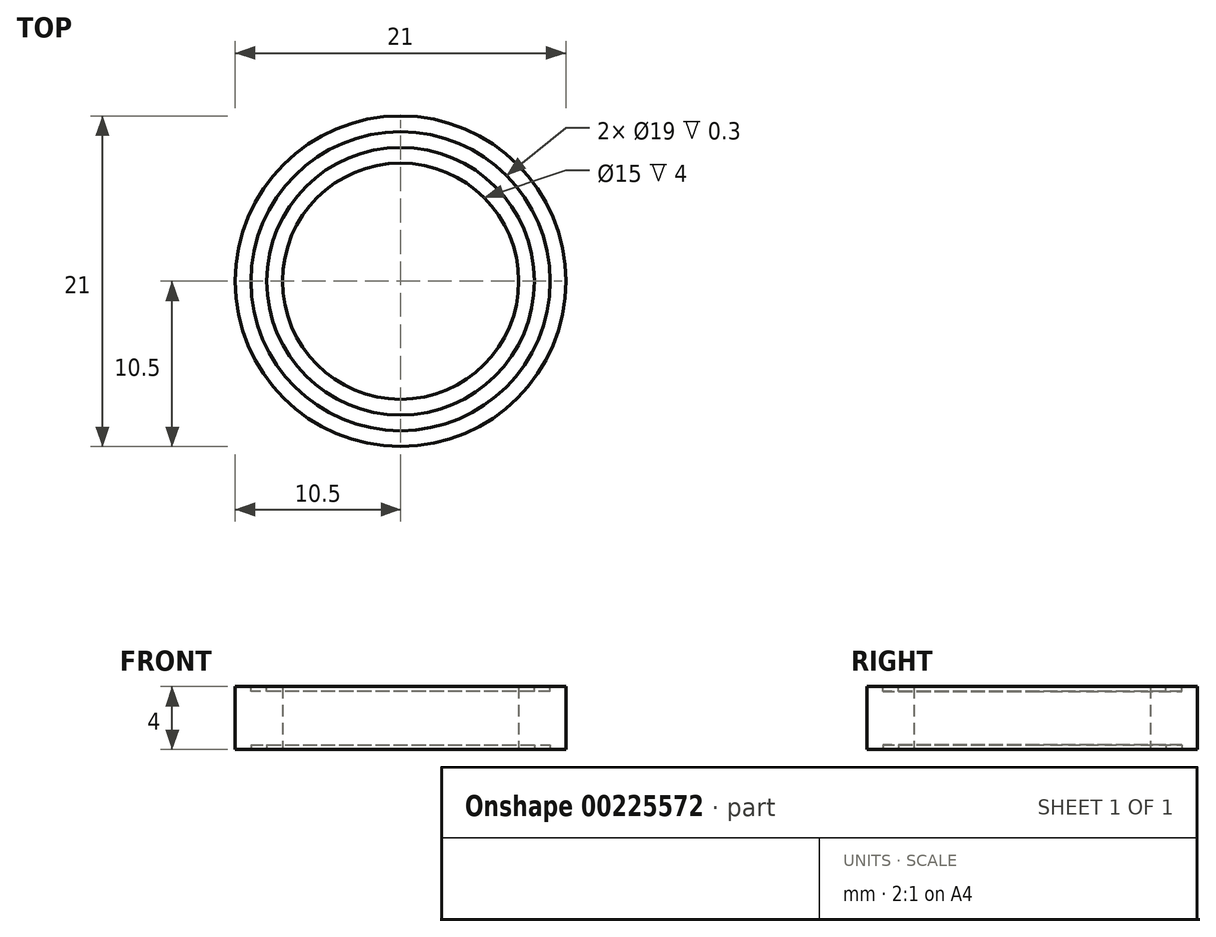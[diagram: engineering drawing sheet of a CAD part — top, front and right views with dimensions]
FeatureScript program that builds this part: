
annotation { "Feature Type Name" : "Feature", "Feature Type Description" : "" }
export const myFeature = defineFeature(function(context is Context, id is Id, definition is map)
    precondition{}
    {
        {
            var Q0;
            Q0=qCreatedBy(makeId("Top.planeOp"),FACE);
            var sketch = newSketch(context, id + "F0", { "sketchPlane" : qUnion([Q0])});
            skCircle(sketch, "E0", {"center": v(0, 0) * mm, "radius": 10.5 * mm});
            skCircle(sketch, "E1", {"center": v(0, 0) * mm, "radius": 7.5 * mm});
            skSolve(sketch);
        }
        {
            var Q0;
            Q0=makeQuery(id+"F0.imprint","IMPRINT",FACE,{"disambiguationData":[TD([[makeQuery(id+"F0.imprint","IMPRINT",EDGE,{"derivedFrom":sQuery(id+"F0.wireOp",EDGE,"E0")}),1.0]])]});
            extrude(context, id + "F1", {"entities" : qUnion([Q0]), "depth" : 4 * mm});
        }
        {
            var Q0;
            Q0=makeQuery(id+"F1.opExtrude","CAP_FACE",FACE,{"disambiguationData":[OSD([sQuery(id+"F0.wireOp",EDGE,"E0"),sQuery(id+"F0.wireOp",EDGE,"E1")])],"isStart":false});
            var sketch = newSketch(context, id + "F2", { "sketchPlane" : qUnion([Q0])});
            skCircle(sketch, "E2", {"center": v(0, 0) * mm, "radius": 9.5 * mm});
            skCircle(sketch, "E3", {"center": v(0, 0) * mm, "radius": 8.5 * mm});
            skSolve(sketch);
        }
        {
            var Q0;
            Q0=makeQuery(id+"F2.imprint","IMPRINT",FACE,{"disambiguationData":[TD([[makeQuery(id+"F2.imprint","IMPRINT",EDGE,{"derivedFrom":sQuery(id+"F2.wireOp",EDGE,"E2")}),1.0]])]});
            extrude(context, id + "F3", {"entities" : qUnion([Q0]), "operationType" : NewBodyOperationType.REMOVE, "oppositeDirection" : true, "depth" : 0.3 * mm});
        }
        {
            var Q0;
            Q0=makeQuery(id+"F1.opExtrude","CAP_FACE",FACE,{"disambiguationData":[OSD([sQuery(id+"F0.wireOp",EDGE,"E0"),sQuery(id+"F0.wireOp",EDGE,"E1")])],"isStart":true});
            var sketch = newSketch(context, id + "F4", { "sketchPlane" : qUnion([Q0])});
            skCircle(sketch, "E4", {"center": v(0, 0) * mm, "radius": 8.5 * mm});
            skCircle(sketch, "E5", {"center": v(0, 0) * mm, "radius": 9.5 * mm});
            skSolve(sketch);
        }
        {
            var Q0;
            Q0=makeQuery(id+"F4.imprint","IMPRINT",FACE,{"disambiguationData":[TD([[makeQuery(id+"F4.imprint","IMPRINT",EDGE,{"derivedFrom":sQuery(id+"F4.wireOp",EDGE,"E4")}),-1.0]])]});
            extrude(context, id + "F5", {"entities" : qUnion([Q0]), "operationType" : NewBodyOperationType.REMOVE, "oppositeDirection" : true, "depth" : 0.3 * mm});
        }
    });
